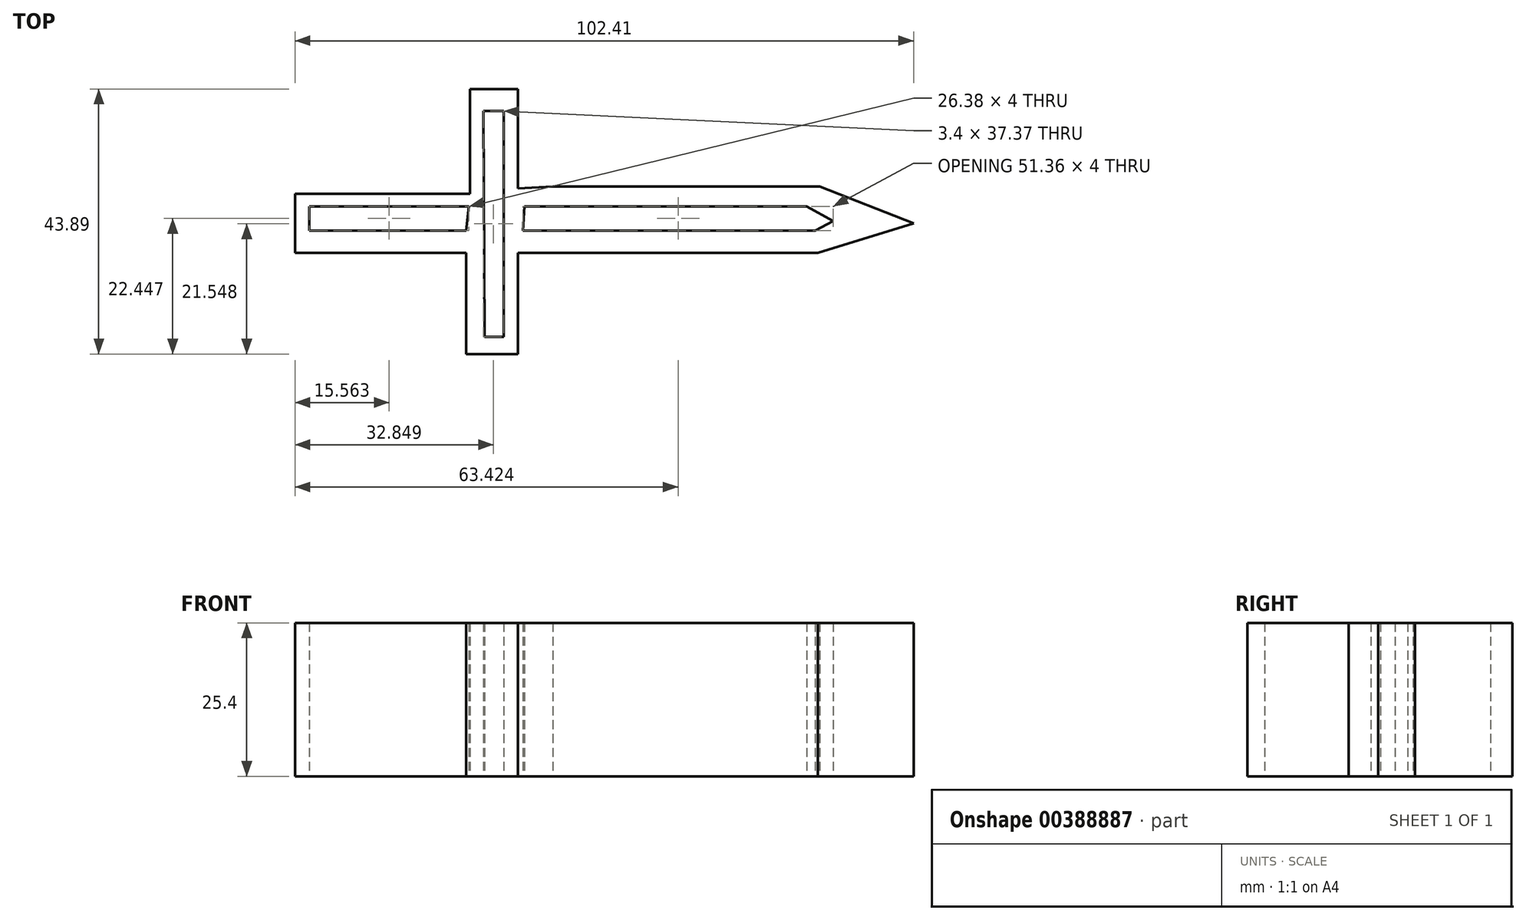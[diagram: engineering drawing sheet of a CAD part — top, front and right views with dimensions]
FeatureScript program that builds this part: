
annotation { "Feature Type Name" : "Feature", "Feature Type Description" : "" }
export const myFeature = defineFeature(function(context is Context, id is Id, definition is map)
    precondition{}
    {
        {
            var Q0;
            Q0=qCreatedBy(makeId("Top.planeOp"),FACE);
            var sketch = newSketch(context, id + "F0", { "sketchPlane" : qUnion([Q0])});
            skPoint(sketch, "E0.17.internal.orphan", {"position": v(0, 30.27) * mm});
            skPoint(sketch, "E1.start.orphan", {"position": v(39.52, 17.84) * mm});
            skPoint(sketch, "E2.start.orphan", {"position": v(44.45, 12.92) * mm});
            skPoint(sketch, "E3.start.orphan", {"position": v(49.37, 17.84) * mm});
            skPoint(sketch, "E4.end.orphan", {"position": v(49.37, 8) * mm});
            skPoint(sketch, "E4.start.orphan", {"position": v(54.3, 12.92) * mm});
            skPoint(sketch, "E5.end.orphan", {"position": v(34.6, 12.92) * mm});
            skLineSegment(sketch, "E6", {"start": v(-5.8, -23.32) * mm, "end": v(38.4, -23.32) * mm});
            skLineSegment(sketch, "E7", {"start": v(38.4, -23.32) * mm, "end": v(53.95, -29.41) * mm});
            skLineSegment(sketch, "E8", {"start": v(53.95, -29.41) * mm, "end": v(38.1, -34.3) * mm});
            skLineSegment(sketch, "E9", {"start": v(38.1, -34.3) * mm, "end": v(-11.58, -34.3) * mm});
            skLineSegment(sketch, "E10", {"start": v(-11.58, -34.3) * mm, "end": v(-11.58, -51.05) * mm});
            skLineSegment(sketch, "E11", {"start": v(-11.58, -51.05) * mm, "end": v(-20.12, -51.05) * mm});
            skLineSegment(sketch, "E12", {"start": v(-20.12, -51.05) * mm, "end": v(-20.12, -34.3) * mm});
            skLineSegment(sketch, "E13", {"start": v(-20.12, -34.3) * mm, "end": v(-48.46, -34.3) * mm});
            skLineSegment(sketch, "E14", {"start": v(-48.46, -34.3) * mm, "end": v(-48.46, -24.54) * mm});
            skLineSegment(sketch, "E15", {"start": v(-48.46, -24.54) * mm, "end": v(-19.5, -24.54) * mm});
            skLineSegment(sketch, "E16", {"start": v(-19.5, -24.54) * mm, "end": v(-19.5, -7.16) * mm});
            skLineSegment(sketch, "E17", {"start": v(-19.5, -7.16) * mm, "end": v(-11.58, -7.16) * mm});
            skLineSegment(sketch, "E18", {"start": v(-11.58, -7.16) * mm, "end": v(-11.58, -23.62) * mm});
            skLineSegment(sketch, "E19", {"start": v(-11.58, -23.62) * mm, "end": v(-5.8, -23.32) * mm});
            skLineSegment(sketch, "E20", {"start": v(-10.52, -26.6) * mm, "end": v(36.25, -26.6) * mm});
            skLineSegment(sketch, "E21", {"start": v(36.25, -26.6) * mm, "end": v(40.64, -29) * mm});
            skLineSegment(sketch, "E22", {"start": v(40.64, -29) * mm, "end": v(37.65, -30.6) * mm});
            skLineSegment(sketch, "E23", {"start": v(37.65, -30.6) * mm, "end": v(-10.72, -30.6) * mm});
            skLineSegment(sketch, "E24", {"start": v(-10.72, -30.6) * mm, "end": v(-10.52, -26.6) * mm});
            skLineSegment(sketch, "E25", {"start": v(-17.3, -10.82) * mm, "end": v(-13.91, -10.82) * mm});
            skLineSegment(sketch, "E26", {"start": v(-13.91, -10.82) * mm, "end": v(-13.91, -48.19) * mm});
            skLineSegment(sketch, "E27", {"start": v(-13.91, -48.19) * mm, "end": v(-17.11, -48.19) * mm});
            skLineSegment(sketch, "E28", {"start": v(-17.11, -48.19) * mm, "end": v(-17.3, -10.82) * mm});
            skLineSegment(sketch, "E29", {"start": v(-19.7, -26.6) * mm, "end": v(-46.09, -26.6) * mm});
            skLineSegment(sketch, "E30", {"start": v(-46.09, -26.6) * mm, "end": v(-46.09, -30.6) * mm});
            skLineSegment(sketch, "E31", {"start": v(-46.09, -30.6) * mm, "end": v(-20.1, -30.6) * mm});
            skLineSegment(sketch, "E32", {"start": v(-20.1, -30.6) * mm, "end": v(-19.7, -26.6) * mm});
            skSolve(sketch);
        }
        {
            var Q0;
            Q0 = qSketchRegion(id + "F0", true);
            extrude(context, id + "F1", {"entities" : qUnion([Q0]), "depth" : 25.4 * mm});
        }
    });
